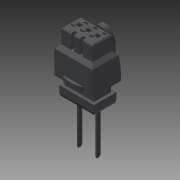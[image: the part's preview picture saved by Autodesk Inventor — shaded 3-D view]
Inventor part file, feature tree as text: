
AUTODESK INVENTOR PART (.ipt)
format: ipt  version: 2018 (Build 220112000, 112)  size: 283,648 bytes
history: native  units: mm
features: extrude x22, sketch x22, other x7
ambient origin geometry x8: Origin, YZ Plane, XZ Plane, XY Plane, X Axis, Y Axis, Z Axis, Center Point
bodies: Solid1 (feature_tree)
feature tree (51):
  extrude  "Extrusion1"  Depth=12.0mm TaperAngle=0.0deg
  extrude  "Extrusion2"  Depth=4.0mm TaperAngle=0.0deg
  extrude  "Extrusion3"  Depth=1.0mm TaperAngle=0.0deg
  extrude  "Extrusion4"  Depth=3.2mm TaperAngle=0.0deg
  extrude  "Extrusion5"  Depth=2.9mm TaperAngle=0.0deg
  extrude  "Extrusion6"  Depth=2.9mm TaperAngle=0.0deg
  extrude  "Extrusion7"  Depth=2.9mm TaperAngle=0.0deg
  extrude  "Extrusion8"  Depth=2.9mm TaperAngle=0.0deg
  extrude  "Extrusion9"  Depth=2.9mm TaperAngle=0.0deg
  extrude  "Extrusion10"  Depth=10.0mm TaperAngle=0.0deg
  extrude  "Extrusion11"  Depth=5.0mm TaperAngle=0.0deg
  extrude  "Extrusion12"  [1 undecoded]
  extrude  "Extrusion13"  [1 undecoded]
  extrude  "Extrusion14"  [1 undecoded]
  extrude  "Extrusion15"  [1 undecoded]
  extrude  "Extrusion16"  [1 undecoded]
  extrude  "Extrusion17"  [1 undecoded]
  extrude  "Extrusion18"  [1 undecoded]
  extrude  "Extrusion19"  [1 undecoded]
  extrude  "Extrusion20"  [1 undecoded]
  extrude  "Extrusion21"  [1 undecoded]
  extrude  "Extrusion22"  [1 undecoded]
  other  "NEBV_XY"
  other  "NEBV_YZ"
  other  "NEBV_ZX"
  other  "NEBV_X"
  other  "NEBV_Y"
  other  "NEBV_Z"
  other  "NEBV_Center"
  sketch  "Sketch_9"  dims[d32=2.9mm d33=0.0mm d34=1.1mm d35=0.0mm]
  sketch  "Sketch_23"
  sketch  "Sketch_1"  dims[d0=8.3mm d1=0.0mm d2=12.0mm d3=0.0mm]
  sketch  "Sketch_2"  dims[d4=2.0mm d5=0.0mm d6=4.0mm d7=0.0mm]
  sketch  "Sketch_3"  dims[d8=3.0mm d9=0.0mm d10=1.0mm d11=0.0mm]
  sketch  "Sketch_4"  dims[d12=1.0mm d13=0.0mm d14=3.2mm d15=0.0mm]
  sketch  "Sketch_5"  dims[d16=2.9mm d17=0.0mm d18=2.9mm d19=0.0mm]
  sketch  "Sketch_6"  dims[d20=2.9mm d21=0.0mm d22=2.9mm d23=0.0mm]
  sketch  "Sketch_19"
  sketch  "Sketch_20"
  sketch  "Sketch_21"
  sketch  "Sketch_7"  dims[d24=2.9mm d25=0.0mm d26=2.9mm d27=0.0mm]
  sketch  "Sketch_8"  dims[d28=2.9mm d29=0.0mm d30=2.9mm d31=0.0mm]
  sketch  "Sketch_10"  dims[d36=6.0mm d37=0.0mm d38=10.0mm d39=0.0mm]
  sketch  "Sketch_11"  dims[d40=10.0mm d41=0.0mm d42=5.0mm d43=0.0mm]
  sketch  "Sketch_12"
  sketch  "Sketch_13"
  sketch  "Sketch_14"
  sketch  "Sketch_15"
  sketch  "Sketch_16"
  sketch  "Sketch_17"
  sketch  "Sketch_18"
note: 11 required parameter values undecoded (feature->parameter linkage not recoverable at this tier; creation-order binding heuristic only, values carry confidence <= 0.55)
